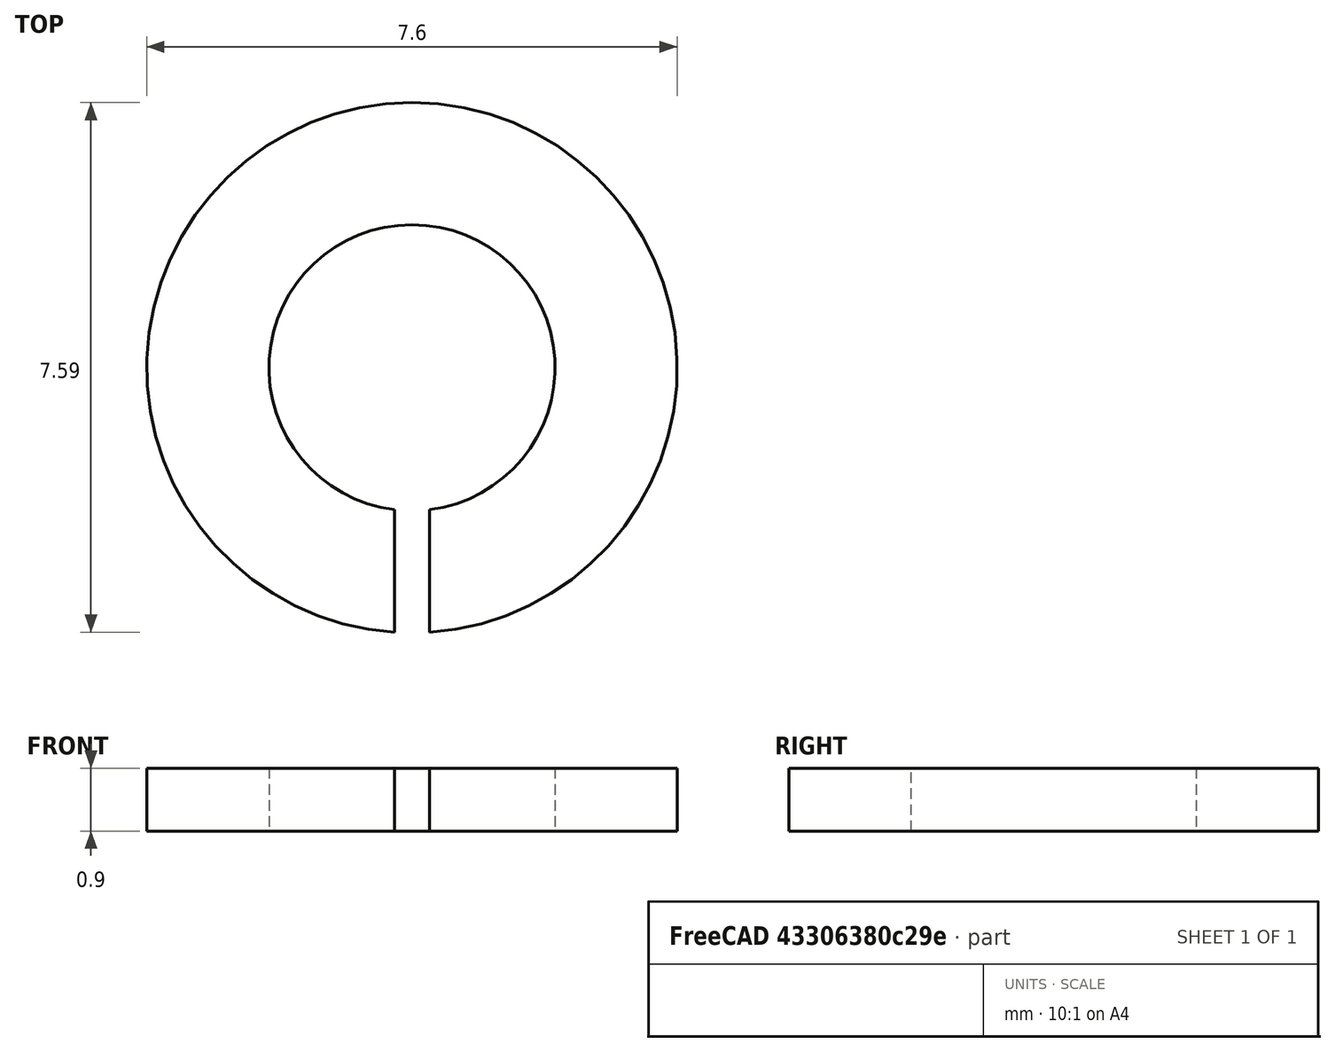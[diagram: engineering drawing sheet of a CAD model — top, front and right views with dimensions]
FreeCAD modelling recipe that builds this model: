
FCSTD DOCUMENT  (FreeCAD 0.15R4651 (Git))
Label: Federring_DIN127-A4
License: All rights reserved
LicenseURL: http://de.wikipedia.org/wiki/Alle_Rechte_vorbehalten
objects: Sketcher::SketchObject×1, PartDesign::Pad×1
note: 3 computed .brp shape members not serialized (recipe doc carries the construction recipe); baked Part::Feature solids carry a one-line shape summary decoded from their .brp

FEATURE [Sketcher::SketchObject] Sketch
  sketch-geometry (4):
    g0: ArcOfCircle CenterX=0 CenterY=0 CenterZ=0 NormalX=0 NormalY=0 NormalZ=1 Radius=2.05 StartAngle=4.83464 EndAngle=10.8733
    g1: ArcOfCircle CenterX=0 CenterY=0 CenterZ=0 NormalX=0 NormalY=0 NormalZ=1 Radius=3.8 StartAngle=4.77823 EndAngle=10.9297
    g2: LineSegment StartX=0.25 StartY=-2.0347 StartZ=0 EndX=0.25 EndY=-3.79177 EndZ=0
    g3: LineSegment StartX=-0.25 StartY=-3.79177 StartZ=0 EndX=-0.25 EndY=-2.0347 EndZ=0
  constraints (12):
    c: Coincident(g0,g-1)
    c: Coincident(g1,g-1)
    c: Vertical(g2)
    c: Vertical(g3)
    c: Coincident(g0,g2)
    c: Coincident(g0,g3)
    c: Coincident(g1,g2)
    c: Coincident(g1,g3)
    c: Symmetric(g1,g1,g-2)
    c: Radius(g0) = 2.05
    c: Radius(g1) = 3.8
    c: DistanceX(g1,g1) = -0.5
FEATURE [PartDesign::Pad] Pad  label="Federring DIN 127-A 4 #"
  Length = 0.9
  Length2 = 100
  Midplane = true
  Sketch = -> Sketch
  Type = 0
